# Revit family: PRD_FrankeWS_WtrSpplFttngsFrWshBsnsAndTrghs_SelfClosingTapMixer_F5SM1003-1005,1008-1010
name_source: partatom
category: Plumbing Fixtures
revit_build: Autodesk Revit 2018 (Build: 20190510_1515(x64)
units: mm (PartAtom-declared; Revit-internal decimal feet)

## family parameters
Cut with Voids When Loaded = No
Host = Face
OmniClass Number = 23.45.55.17
OmniClass Title = Mixing Faucets
Part Type = Normal
Room Calculation Point = No
Round Connector Dimension = Use Diameter
Shared = No

## types (6) — shared parameters
AdjustableFlowTime = yes
AssetType = Fixed
Category = Pr_40_20_87_98, Washbasin taps
Color = Chrome
Default Elevation = 850 mm  [stored 2.78871 ft]
Depressurised = no
DiameterNominal = 15.000 mm
DurationUnit = year
FaucetFunction = MIXED
FaucetOperation = SELFCLOSING
FaucetType = BIB
Features = For sanitary facilities. Connects to hot and cold water, high-polished chromium-plated brass.
Finish = high-polished chromium-plated brass
FlowColdWater = 0.1 L/s
FlowHotWater = 0.1 L/s
HygieneFlushing = no
IfcExportAs = IfcValveType
IfcExportType = FAUCET
InletSize = G-1-2-B
Manufacturer = KWC Group AG
ManufacturerName = KWC Group AG
ManufacturerURL = www.kwc.com
Material = Brass
MaximumFlowTime = 35.00 seconds
MinimumFlowPressure = 0.50 bar
MinimumFlowTime = 5.00 seconds
NBSDescription = Water supply fittings for wash basins and troughs
NBSReference = 45-35-70/371
NominalWidth = 223 mm  [stored 0.731627 ft]
OutletMaterial = PRD_AR_SyntheticGrey
ProductInformation = https://pim.kwc.com
ProtectiveShutdown = no
SoundInsulation = no
TapBottomOffset = 65.5 mm  [stored 0.214895 ft]
TapMaterial = PRD_AR_ChromatedBrass_HighPolished
ThermalDisinfection = no
TypeOfMixing = with mixer
TypeOfMounting = Wall mounting
TypeOfOperation = manual operation
TypeOfTap = bib tap
URL = www.kwc.com
Uniclass2015Code = Pr_40_20_87_98
Uniclass2015Title = Washbasin taps
Uniclass2015Version = Products v1.10
Version = 1
WarrantyDurationUnit = year
zero-valued in all types: NominalHeight, NominalLength

## per-type parameters (varying)
| type | BIMObjectName | Description | FunctionalPrinciple | GrossWeight | LengthToSpout | Model | ModelNumber | ModelReference | Name | NetWeight | SpoutProjection | VolumeFlowRate |
| F5SM1003 - 0.10 L/s, projection 135 mm | PRD_AR_WaterSupplyFittingsForWashBasinsAndTroughs_SelfClosingTapMixer_F5SM1003 | F5S mix self-closing wall-mounted mixer DN 15 as single-mixer tap for wall mounting with lockable swivelling spout, for sanitary facilities. FRAMIC self-closing mixing cartridge, hydraulically controlled, low-maintenance and stagnation-free, with ceramic disc technology, self-closing, flow pressure-independent due to medium-separated design. Stepless adjustment of flow duration. With adjustable, turn-proof temperature stop. Connects to hot and cold water. All-metal construction, high-polished chromium-plated brass. Laminar jet controller with integrated flow regulator 6.0 l/min. With adjustable and lockable connections with backflow preventer and strainers, completely covered with depth-adjustable screw rosettes. Projection 135 mm. | ;hydraulic self-closing | 4.00 kg | 135 mm  [stored 0.442913 ft] | F5SM1003 | 2030032991 | F5SM1003 | F5 self-closing tap mixer F5SM1003 | 3.90 kg | 135.00 mm | 0.10 L/s at 3 bar |
| F5SM1004 - 0.10 L/s, projection 195 mm | PRD_AR_WaterSupplyFittingsForWashBasinsAndTroughs_SelfClosingTapMixer_F5SM1004 | F5S mix self-closing wall-mounted mixer DN 15 as single-mixer tap for wall mounting with lockable swivelling spout, for sanitary facilities. FRAMIC self-closing mixing cartridge, hydraulically controlled, low-maintenance and stagnation-free, with ceramic disc technology, self-closing, flow pressure-independent due to medium-separated design. Stepless adjustment of flow duration. With adjustable, turn-proof temperature stop. Connects to hot and cold water. All-metal construction, high-polished chromium-plated brass. Laminar jet controller with integrated flow regulator 6.0 l/min. With adjustable and lockable connections with backflow preventer and strainers, completely covered with depth-adjustable screw rosettes. Projection 195 mm. | ;hydraulic self-closing | 4.00 kg | 195 mm  [stored 0.639764 ft] | F5SM1004 | 2030032992 | F5SM1004 | F5 self-closing tap mixer F5SM1004 | 3.90 kg | 195.00 mm | 0.10 L/s at 3 bar |
| F5SM1005 - 0.10 L/s, projection 255 mm | PRD_AR_WaterSupplyFittingsForWashBasinsAndTroughs_SelfClosingTapMixer_F5SM1005 | F5S mix self-closing wall-mounted mixer DN 15 as single-mixer tap for wall mounting with lockable swivelling spout, for sanitary facilities. FRAMIC self-closing mixing cartridge, hydraulically controlled, low-maintenance and stagnation-free, with ceramic disc technology, self-closing, flow pressure-independent due to medium-separated design. Stepless adjustment of flow duration. With adjustable, turn-proof temperature stop. Connects to hot and cold water. All-metal construction, high-polished chromium-plated brass. Laminar jet controller with integrated flow regulator 6.0 l/min. With adjustable and lockable connections with backflow preventer and strainers, completely covered with depth-adjustable screw rosettes. Projection 255 mm. | ;hydraulic self-closing | 4.40 kg | 255 mm  [stored 0.836614 ft] | F5SM1005 | 2030032993 | F5SM1005 | F5 self-closing tap mixer F5SM1005 | 4.18 kg | 255.00 mm | 0.10 L/s at 3 bar |
| F5SM1008 - 0.05 L/s, projection 135 mm | PRD_AR_WaterSupplyFittingsForWashBasinsAndTroughs_SelfClosingTapMixer_F5SM1008 | F5S mix self-closing wall-mounted mixer DN 15 as single-mixer tap for wall mounting with lockable swivelling spout, for sanitary facilities. FRAMIC self-closing mixing cartridge, hydraulically controlled, low-maintenance and stagnation-free, with ceramic disc technology, self-closing, flow pressure-independent due to medium-separated design. Stepless adjustment of flow duration. With adjustable, turn-proof temperature stop. Connects to hot and cold water. All-metal construction, high-polished chromium-plated brass. Aerator with an integrated flow regulator 3.0 l/min. With adjustable and lockable connections with backflow preventer and strainers, completely covered with depth-adjustable screw rosettes. Projection 135 mm. | hydraulic self-closing | 4.30 kg | 135 mm  [stored 0.442913 ft] | F5SM1008 | 2030040314 | F5SM1008 | F5 self-closing tap mixer F5SM1008 | 4.09 kg | 135.00 mm | 0.05 L/s at 3 bar |
| F5SM1009 - 0.05 L/s, projection 195 mm | PRD_AR_WaterSupplyFittingsForWashBasinsAndTroughs_SelfClosingTapMixer_F5SM1009 | F5S mix self-closing wall-mounted mixer DN 15 as single-mixer tap for wall mounting with lockable swivelling spout, for sanitary facilities. FRAMIC self-closing mixing cartridge, hydraulically controlled, low-maintenance and stagnation-free, with ceramic disc technology, self-closing, flow pressure-independent due to medium-separated design. Stepless adjustment of flow duration. With adjustable, turn-proof temperature stop. Connects to hot and cold water. All-metal construction, high-polished chromium-plated brass. Aerator with an integrated flow regulator 3.0 l/min. With adjustable and lockable connections with backflow preventer and strainers, completely covered with depth-adjustable screw rosettes. Projection 195 mm. | ;hydraulic self-closing | 4.35 kg | 195 mm  [stored 0.639764 ft] | F5SM1009 | 2030040316 | F5SM1009 | F5 self-closing tap mixer F5SM1009 | 4.13 kg | 195.00 mm | 0.05 L/s at 3 bar |
| F5SM1010 - 0.05 L/s, projection 255 mm | PRD_AR_WaterSupplyFittingsForWashBasinsAndTroughs_SelfClosingTapMixer_F5SM1010 | F5S mix self-closing wall-mounted mixer DN 15 as single-mixer tap for wall mounting with lockable swivelling spout, for sanitary facilities. FRAMIC self-closing mixing cartridge, hydraulically controlled, low-maintenance and stagnation-free, with ceramic disc technology, self-closing, flow pressure-independent due to medium-separated design. Stepless adjustment of flow duration. With adjustable, turn-proof temperature stop. Connects to hot and cold water. All-metal construction, high-polished chromium-plated brass. Aerator with an integrated flow regulator 3.0 l/min. With adjustable and lockable connections with backflow preventer and strainers, completely covered with depth-adjustable screw rosettes. Projection 255 mm. | hydraulic self-closing | 4.40 kg | 255 mm  [stored 0.836614 ft] | F5SM1010 | 2030040317 | F5SM1010 | F5 self-closing tap mixer F5SM1010 | 4.18 kg | 255.00 mm | 0.05 L/s at 3 bar |

note: [stored X ft] marks values corroborated as IEEE doubles in the binary element streams (Revit-internal decimal feet)

## geometry (parser evidence)
native form markers: Sweep x4
no freeform markers — native parametric forms only
